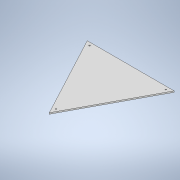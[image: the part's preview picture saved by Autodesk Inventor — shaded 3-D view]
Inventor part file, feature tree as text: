
AUTODESK INVENTOR PART (.ipt)
format: ipt  version: 2020 (Build 240168000, 168)  size: 97,280 bytes
history: native  units: in
note: dims shown in document units (in); Inventor stores cm internally (conversion verified against a paired STEP export)
features: extrude x1, sketch x1
ambient origin geometry x8: Origin, YZ Plane, XZ Plane, XY Plane, X Axis, Y Axis, Z Axis, Center Point
bodies: Solid1 (feature_tree)
feature tree (2):
  extrude  "Extrusion1"  [1 undecoded]
  sketch  "Sketch1"  dims[d0=0.0787in d1=0.0in]
note: 1 required parameter value undecoded (feature->parameter linkage not recoverable at this tier; creation-order binding heuristic only, values carry confidence <= 0.55)
